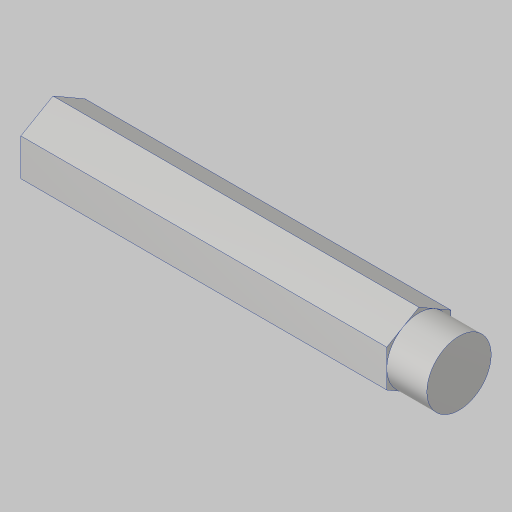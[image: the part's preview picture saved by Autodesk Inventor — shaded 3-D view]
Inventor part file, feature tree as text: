
AUTODESK INVENTOR PART (.ipt)
format: ipt  version: 2023.5 (Build 275446000, 446)  size: 114,176 bytes
history: native  units: in
note: dims shown in document units (in); Inventor stores cm internally (conversion verified against a paired STEP export)
features: extrude x2, sketch x2, projected_geometry x1
ambient origin geometry x8: Origin, YZ Plane, XZ Plane, XY Plane, X Axis, Y Axis, Z Axis, Center Point
bodies: Solid1 (feature_tree)
feature tree (5):
  extrude  "Extrusion1"  Depth=3.163in TaperAngle=0.0deg
  extrude  "Extrusion2"  Depth=0.3125in TaperAngle=0.0deg
  sketch  "Sketch1"  dims[d0=0.5in d1=3.163in d2=0.0in]
  sketch  "Sketch2"  dims[d3=0.5in d4=0.3125in d5=0.0in]
  projected_geometry  "Projected Loop1"
